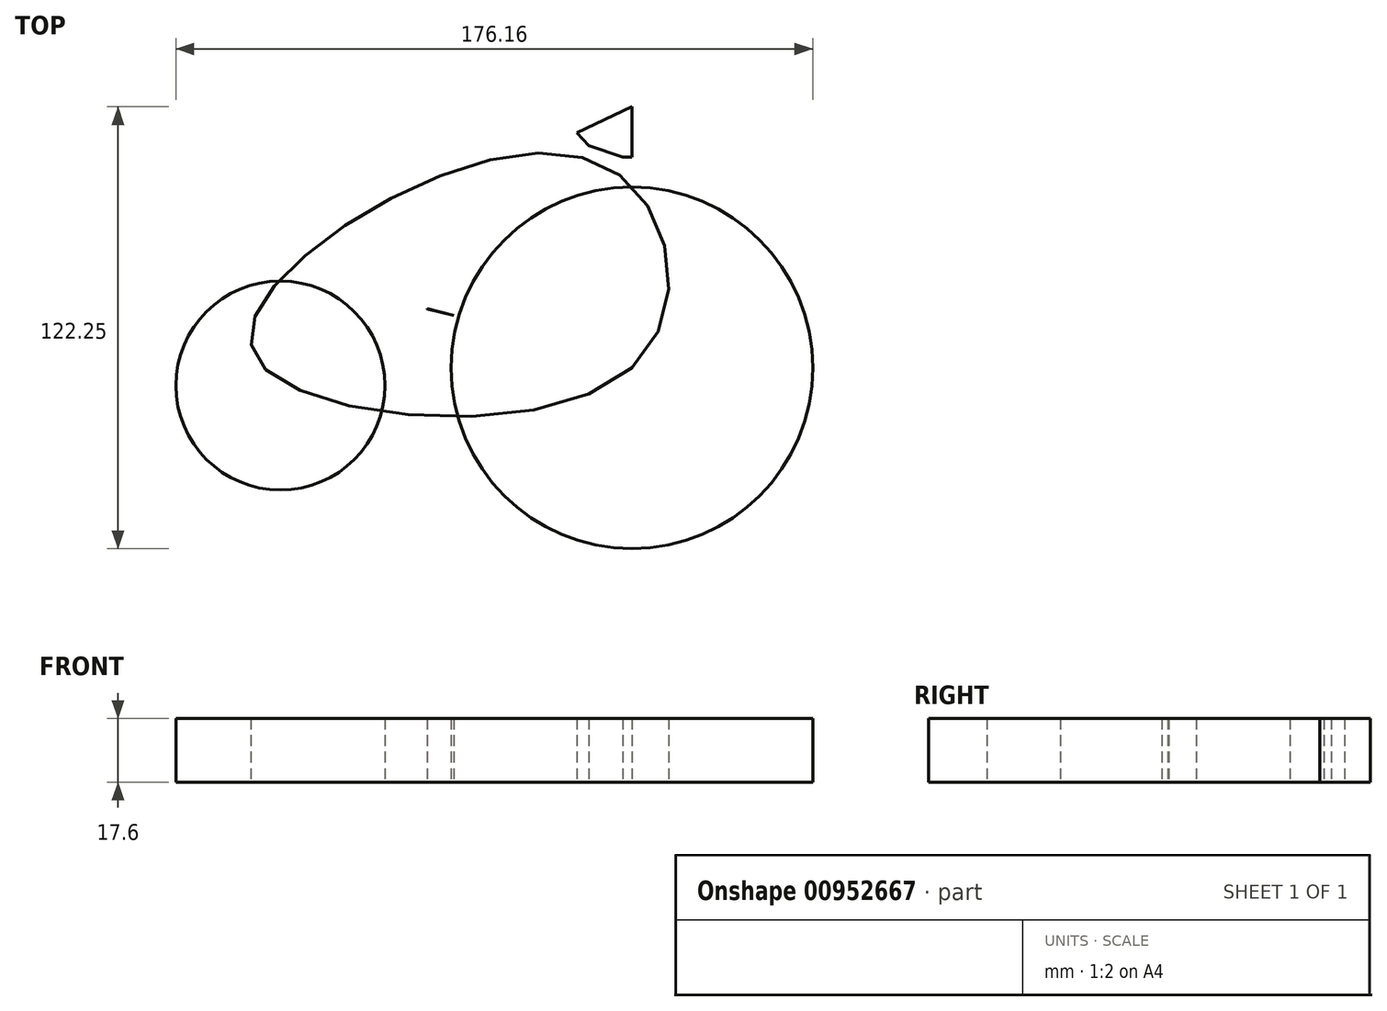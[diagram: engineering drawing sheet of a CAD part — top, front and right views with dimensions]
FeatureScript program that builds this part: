
annotation { "Feature Type Name" : "Feature", "Feature Type Description" : "" }
export const myFeature = defineFeature(function(context is Context, id is Id, definition is map)
    precondition{}
    {
        {
            var Q0;
            Q0=qCreatedBy(makeId("Top.planeOp"),FACE);
            var sketch = newSketch(context, id + "F0", { "sketchPlane" : qUnion([Q0])});
            skCircle(sketch, "E0", {"center": v(0, 0) * mm, "radius": 50 * mm});
            skSolve(sketch);
        }
        {
            var Q0;
            Q0=qCreatedBy(makeId("Top.planeOp"),FACE);
            var sketch = newSketch(context, id + "F1", { "sketchPlane" : qUnion([Q0])});
            skFitSpline(sketch, "E1", {"points": [v(0, 0) * mm, v(-5.3, 54.67) * mm, v(-86.45, 34.28) * mm, v(-101.84, 0) * mm, v(0, 0) * mm]});
            skSolve(sketch);
        }
        {
            var Q0;
            Q0=qCreatedBy(makeId("Top.planeOp"),FACE);
            var sketch = newSketch(context, id + "F2", { "sketchPlane" : qUnion([Q0])});
            skCircle(sketch, "E2", {"center": v(-97.24, -4.9) * mm, "radius": 28.92 * mm});
            skLineSegment(sketch, "E3", {"start": v(-49.27, 48.87) * mm, "end": v(-49.27, 63.86) * mm});
            skLineSegment(sketch, "E4", {"start": v(-49.27, 63.86) * mm, "end": v(-38.88, 67.86) * mm});
            skLineSegment(sketch, "E5", {"start": v(-38.88, 67.86) * mm, "end": v(-63.66, 58.66) * mm});
            skLineSegment(sketch, "E6", {"start": v(0, 0) * mm, "end": v(0, 72.25) * mm});
            skLineSegment(sketch, "E7", {"start": v(0, 72.25) * mm, "end": v(-15.3, 65.06) * mm});
            skLineSegment(sketch, "E8", {"start": v(-15.3, 65.06) * mm, "end": v(-11.9, 61.46) * mm});
            skLineSegment(sketch, "E9", {"start": v(-11.9, 61.46) * mm, "end": v(-2.5, 58.26) * mm});
            skLineSegment(sketch, "E10", {"start": v(-2.5, 58.26) * mm, "end": v(6.5, 58.26) * mm});
            skLineSegment(sketch, "E11", {"start": v(6.5, 58.26) * mm, "end": v(12.5, 58.26) * mm});
            skLineSegment(sketch, "E12", {"start": v(-49.27, 48.87) * mm, "end": v(-56.68, 16.22) * mm});
            skLineSegment(sketch, "E13", {"start": v(-56.68, 16.22) * mm, "end": v(-49.27, 14.54) * mm});
            skLineSegment(sketch, "E14", {"start": v(-49.27, 14.54) * mm, "end": v(-65.37, 18.7) * mm});
            skSolve(sketch);
        }
        {
            var Q0;
            Q0 = qSketchRegion(id + "F0", true);
            var Q1;
            Q1 = qSketchRegion(id + "F1", true);
            var Q2;
            Q2 = qSketchRegion(id + "F2", true);
            extrude(context, id + "F3", {"entities" : qUnion([Q0, Q1, Q2]), "depth" : 17.6 * mm, "offsetDistance" : 25 * mm});
        }
    });
